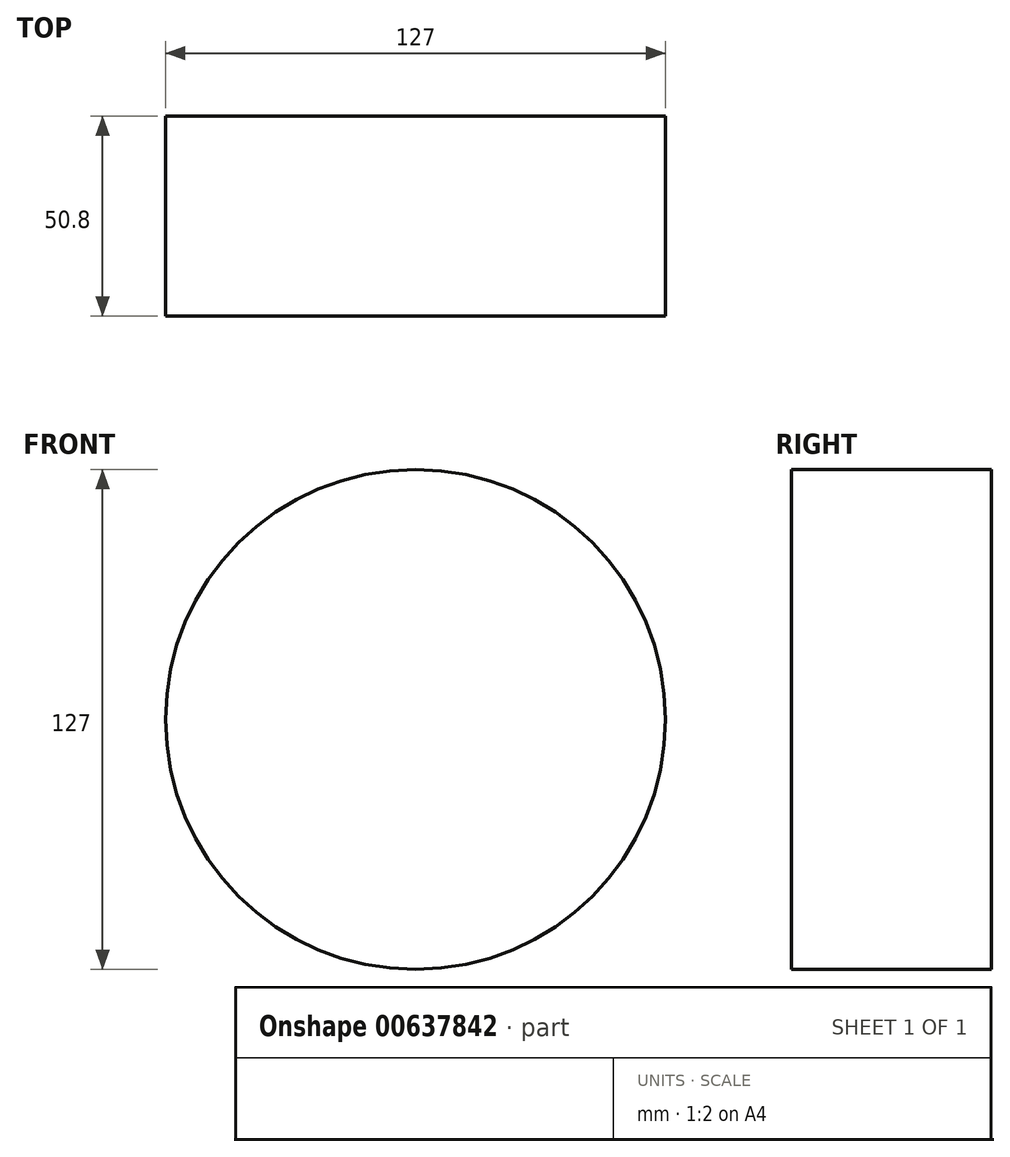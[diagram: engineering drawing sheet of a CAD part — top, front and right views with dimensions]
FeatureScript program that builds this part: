
annotation { "Feature Type Name" : "Feature", "Feature Type Description" : "" }
export const myFeature = defineFeature(function(context is Context, id is Id, definition is map)
    precondition{}
    {
        {
            var Q0;
            Q0=qCreatedBy(makeId("Front.planeOp"),FACE);
            var sketch = newSketch(context, id + "F0", { "sketchPlane" : qUnion([Q0])});
            skCircle(sketch, "E0", {"center": v(0, 0) * mm, "radius": 63.5 * mm});
            skSolve(sketch);
        }
        {
            var Q0;
            Q0 = qSketchRegion(id + "F0", true);
            extrude(context, id + "F1", {"entities" : qUnion([Q0]), "depth" : 50.8 * mm, "offsetDistance" : 25.4 * mm});
        }
    });
